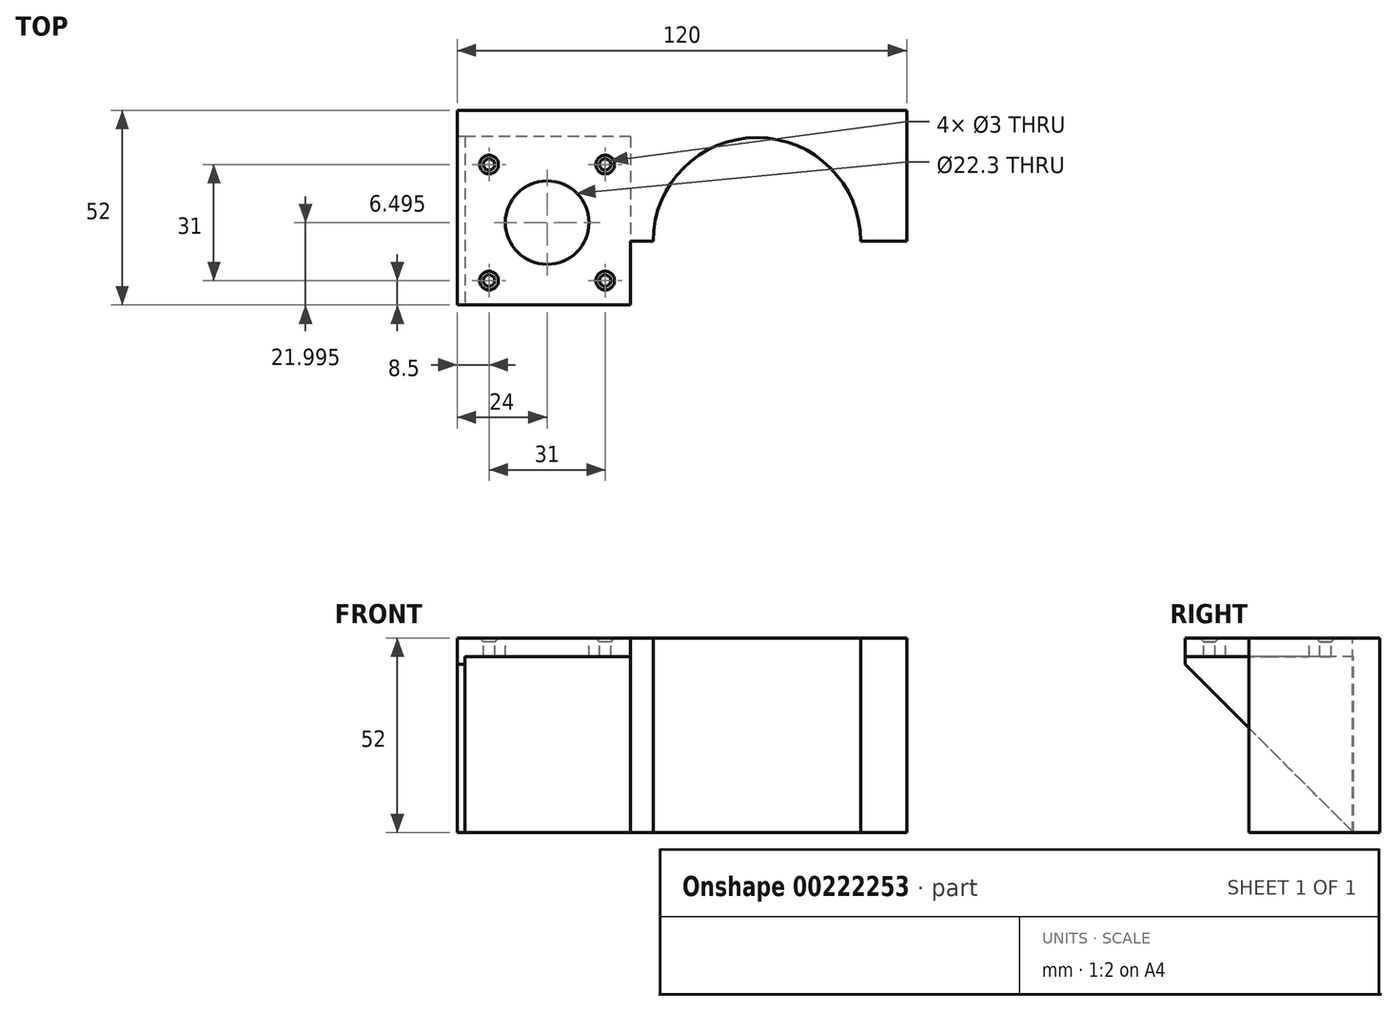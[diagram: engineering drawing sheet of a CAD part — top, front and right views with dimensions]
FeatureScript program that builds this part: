
annotation { "Feature Type Name" : "Feature", "Feature Type Description" : "" }
export const myFeature = defineFeature(function(context is Context, id is Id, definition is map)
    precondition{}
    {
        {
            var Q0;
            Q0=qCreatedBy(makeId("Top.planeOp"),FACE);
            var sketch = newSketch(context, id + "F0", { "sketchPlane" : qUnion([Q0])});
            skLineSegment(sketch, "E0.top", {"start": v(60, 30.77) * mm, "end": v(-60, 30.77) * mm});
            skLineSegment(sketch, "E0.left", {"start": v(60, -4.23) * mm, "end": v(60, 30.77) * mm});
            skLineSegment(sketch, "E0.right", {"start": v(-60, -21.23) * mm, "end": v(-60, 30.77) * mm});
            skArc(sketch, "E1", {"start": v(47.7, -4.23) * mm, "mid": v(20, 23.47) * mm, "end": v(-7.7, -4.23) * mm});
            skCircle(sketch, "E2", {"center": v(-36, 0.77) * mm, "radius": 11.15 * mm});
            skPoint(sketch, "E3", {"position": v(-51.5, 16.27) * mm});
            skPoint(sketch, "E4", {"position": v(-51.5, -14.73) * mm});
            skPoint(sketch, "E5", {"position": v(-20.5, -14.73) * mm});
            skPoint(sketch, "E6", {"position": v(-20.5, 16.27) * mm});
            skLineSegment(sketch, "E7", {"start": v(-13.7, -4.23) * mm, "end": v(-13.7, -21.23) * mm});
            skLineSegment(sketch, "E8", {"start": v(-13.7, -21.23) * mm, "end": v(-60, -21.23) * mm});
            skLineSegment(sketch, "E9", {"start": v(-13.7, -4.23) * mm, "end": v(-7.7, -4.23) * mm});
            skLineSegment(sketch, "E10.trimOffspring", {"start": v(47.7, -4.23) * mm, "end": v(60, -4.23) * mm});
            skSolve(sketch);
        }
        {
            var Q0;
            Q0=makeQuery(id+"F0.imprint","IMPRINT",FACE,{"disambiguationData":[TD([[makeQuery(id+"F0.imprint","IMPRINT",EDGE,{"derivedFrom":sQuery(id+"F0.wireOp",EDGE,"E0.top")}),1.0]])]});
            extrude(context, id + "F1", {"entities" : qUnion([Q0]), "oppositeDirection" : true, "depth" : 52 * mm});
        }
        {
            var Q0;
            Q0=sQuery(id+"F0.wireOp",VERTEX,"E3");
            var Q1;
            Q1=sQuery(id+"F0.wireOp",VERTEX,"E6");
            var Q2;
            Q2=sQuery(id+"F0.wireOp",VERTEX,"E4");
            var Q3;
            Q3=sQuery(id+"F0.wireOp",VERTEX,"E5");
            var Q4;
            Q4=makeQuery(id+"F1.opExtrude","SWEPT_BODY",BODY,{"disambiguationData":[OSD([sQuery(id+"F0.wireOp",EDGE,"E0.top"),sQuery(id+"F0.wireOp",EDGE,"E0.left"),sQuery(id+"F0.wireOp",EDGE,"E0.right"),sQuery(id+"F0.wireOp",EDGE,"E1"),sQuery(id+"F0.wireOp",EDGE,"E2"),sQuery(id+"F0.wireOp",EDGE,"E7"),sQuery(id+"F0.wireOp",EDGE,"E8"),sQuery(id+"F0.wireOp",EDGE,"E9"),sQuery(id+"F0.wireOp",EDGE,"E10.trimOffspring")])]});
            hole(context, id + "F2", {"style" : HoleStyle.C_SINK, "endStyle" : HoleEndStyle.THROUGH, "standardTappedOrClearance" : lookupTablePath({ "standard" : "ISO", "size" : "3", "type" : "Drilled" }), "standardBlindInLast" : lookupTablePath({ "standard" : "ISO", "size" : "3", "type" : "Drilled" }), "holeDiameter" : 3 * mm, "cSinkDiameter" : 5 * mm, "cSinkAngle" : 90 * degree, "locations" : qUnion([Q0, Q1, Q2, Q3]), "scope" : qUnion([Q4]), "isTappedThrough" : true});
        }
        {
            var Q0;
            Q0=makeQuery(id+"F1.opExtrude","SWEPT_FACE",FACE,{"disambiguationData":[OSD([sQuery(id+"F0.wireOp",EDGE,"E8")])]});
            var sketch = newSketch(context, id + "F3", { "sketchPlane" : qUnion([Q0])});
            skLineSegment(sketch, "E11", {"start": v(-13.7, -5) * mm, "end": v(-58, -5) * mm});
            skLineSegment(sketch, "E12", {"start": v(-58, -5) * mm, "end": v(-58, -52) * mm});
            skSolve(sketch);
        }
        {
            var Q0;
            {var subQ0=sQuery(id+"F3.wireOp",EDGE,"E11");Q0=makeQuery(id+"F3.imprint","IMPRINT",FACE,{"disambiguationData":[TD([[makeQuery(id+"F3.imprint","IMPRINT",EDGE,{"derivedFrom":subQ0}),1.0]])]});}
            extrude(context, id + "F4", {"entities" : qUnion([Q0]), "operationType" : NewBodyOperationType.REMOVE, "oppositeDirection" : true, "depth" : 45 * mm});
        }
        {
            var Q0;
            Q0=makeQuery(id+"F1.opExtrude","CAP_EDGE",EDGE,{"disambiguationData":[OSD([sQuery(id+"F0.wireOp",EDGE,"E8")])],"isStart":false});
            chamfer(context, id + "F5", {"entities" : qUnion([Q0]), "width" : 45 * mm});
        }
    });
